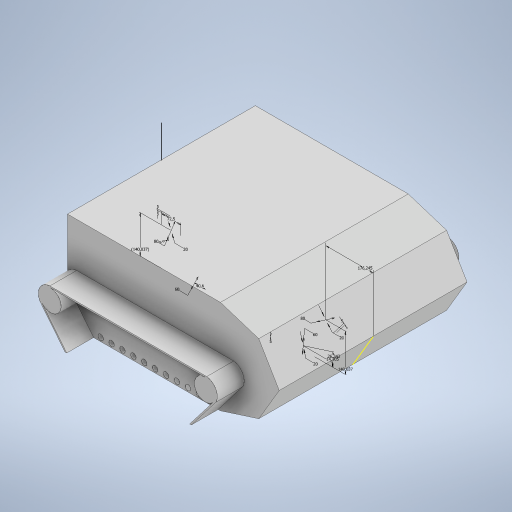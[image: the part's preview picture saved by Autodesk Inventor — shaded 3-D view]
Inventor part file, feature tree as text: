
AUTODESK INVENTOR PART (.ipt)
format: ipt  version: 2023 (Build 270158000, 158)  size: 386,560 bytes
history: native  units: mm
features: extrude x14, sketch x2
ambient origin geometry x8: Origin, YZ Plane, XZ Plane, XY Plane, X Axis, Y Axis, Z Axis, Center Point
bodies: Solido1 (feature_tree)
feature tree (16):
  sketch  "Schizzo1"
  extrude  "Estrusione1"  Depth=600.0mm
  extrude  "Estrusione2"  Depth=350.0mm
  sketch  "Schizzo2"
  extrude  "Estrusione3"  Depth=150.0mm
  extrude  "Estrusione6"  Depth=150.0mm
  extrude  "Estrusione7"  Depth=150.0mm
  extrude  "Estrusione8"  Depth=150.0mm
  extrude  "Estrusione9"  Depth=3.103677mm
  extrude  "Estrusione10"  Depth=10.377397mm
  extrude  "Estrusione11"  Depth=30.0mm
  extrude  "Estrusione12"  Depth=30.0mm
  extrude  "Estrusione13"  Depth=30.0mm
  extrude  "Estrusione14"  Depth=117.867906mm
  extrude  "Estrusione15"  Depth=124.525778mm
  extrude  "Estrusione17"  Depth=700.0mm TaperAngle=0.0deg
